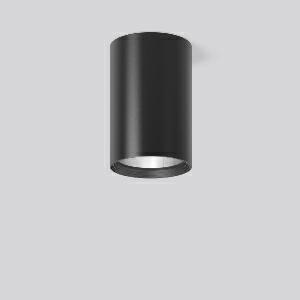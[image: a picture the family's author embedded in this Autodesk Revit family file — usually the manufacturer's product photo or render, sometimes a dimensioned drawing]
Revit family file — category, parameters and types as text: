
# Revit family: heledon_maxi_a_931217_003_76_6bcc
name_source: partatom
category: Lighting Fixtures
units: mm (PartAtom-declared; Revit-internal decimal feet)

## family parameters
Cut with Voids When Loaded = No
Host = Face
Light Source = No
Part Type = Normal
Room Calculation Point = No
Round Connector Dimension = Use Diameter
Shared = No

## types (1)
- HELEDON maxi A (1 x LED Modul 930, 3350 lm, 3000)
    Apparent Load = 25 VA
    Approval mark = CE
    CIE Flux Codes = 100 100 100 100 100
    Color Rendering = 90
    Color Temperature = 3000
    Default Elevation = 1800 mm
    Description = Series: HELEDON maxi
Cylindrical surface-mounted downlight. Housing: die-cast aluminium, powder-coated. Internal ceiling frame polycarbonate with bayonet mounting. Black plastic ring and recessed LED to prevent glare from the side. Optical assembly with reflector made of MIRO-Silver with 98% total light reflection for outstanding efficiency - can be changed without tools. Best colour rendering index Ra>90. Suitable for Ceiling mounting. Easy installation with a separate ceiling frame with bayonet mounting and plug connection. Driver integrated. Connected via plug-in connector. High quality converter without flickering and stroboscopic effect. The following accessories can be mounted without use of tools: interchangeable lenses, decorative glasses, honeycomb louvre, clear and frosted diffusers, white interchangeable plastic ring. 
Colour: deep black, matt (RAL 9005)
Diameter: 123 mm
Height: 183 mm
Lamp: LED
Socket: without socket
Colour temperature: 3000K
Colour rendering index (CRI): 92
System power: 25 W
Rated luminous flux: 3350 lm
Luminous efficiency: 134 lm/W
Control gear: Converter, dimmable, DALI
Protection class: I
Type of protection: IP 20
    Height = 183 mm
    Lamp = 1 x LED Modul 930
    Lamp Light Flux = 3350 lm
    Lamp count = 1
    Length = 123 mm
    Lifetime = 50000 h
    Luminous efficacy = 134 lm/W
    Manufacturer = RZB
    ModVariant = No
    Model = 931217.003.76
    Mounting Place = Ceiling
    Mounting Type = Surface mounted
    Number of Poles = 1
    OnlyDefault = Yes
    Power Factor = 1
    Product Name = HELEDON maxi A
    Product group = Surface mounted downlights
    ProductGroupID = 302
    Protection Class = Protection class I
    Protection Degree = IP 20
    RLX_Detail_Level = 1
    RLX_Emergency_Light_Flux = 0 lm
    RLX_Emergency_Type = 0
    RLX_Emergency_Type_DB = No
    RlxData = <blob elided: 98105 chars, md5=4be97da6>
    Socket = socket
    Standby Power = 0 W
    System Light Flux = 3350 lm
    System Power = 25 W
    Type Comments = Product without accessories
    Type Image = 931192.003.jpg
    URL = http://relux.com
    VarID = ---
    Voltage = 230 V
    Voltage Range = 220-240 V
    Weight = 0.00 kg
    Width = 0 mm  [stored 0 ft]

note: [stored X ft] marks values corroborated as IEEE doubles in the binary element streams (Revit-internal decimal feet)

## geometry (parser evidence)
native form markers: Blend x4, Sweep x9
no freeform markers — native parametric forms only
